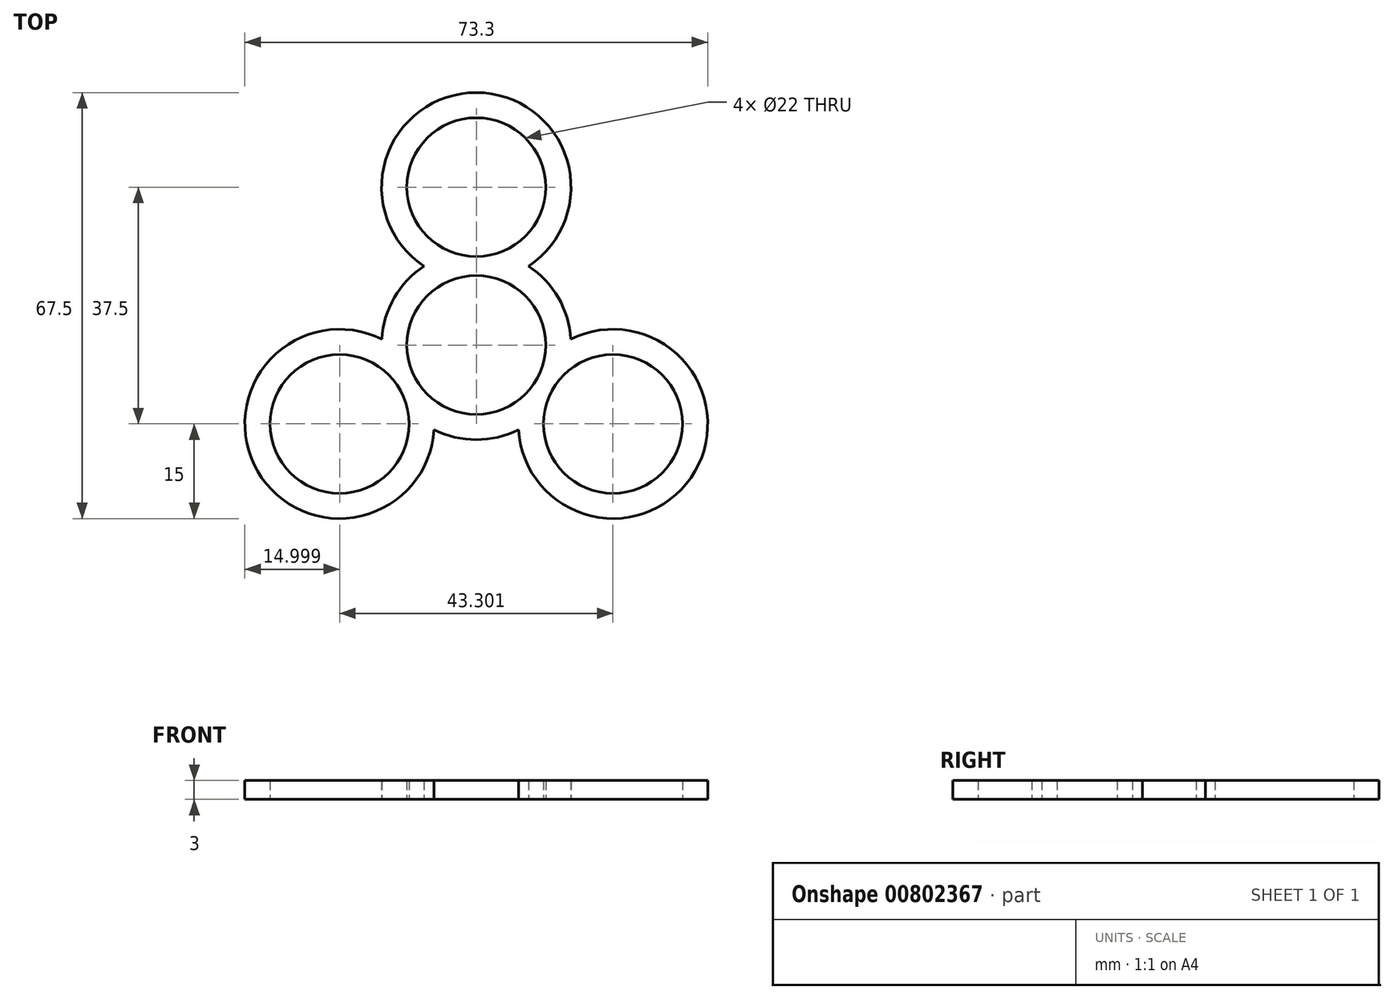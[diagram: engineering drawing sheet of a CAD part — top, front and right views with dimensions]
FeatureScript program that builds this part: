
annotation { "Feature Type Name" : "Feature", "Feature Type Description" : "" }
export const myFeature = defineFeature(function(context is Context, id is Id, definition is map)
    precondition{}
    {
        {
            var Q0;
            Q0=qCreatedBy(makeId("Top.planeOp"),FACE);
            var sketch = newSketch(context, id + "F0", { "sketchPlane" : qUnion([Q0])});
            skArc(sketch, "E0", {"start": v(9.53, 5.5) * mm, "mid": v(0, 11) * mm, "end": v(-9.53, 5.5) * mm});
            skCircle(sketch, "E1", {"center": v(0, 25) * mm, "radius": 11 * mm});
            skArc(sketch, "E2", {"start": v(8.3, 12.5) * mm, "mid": v(0, 40) * mm, "end": v(-8.3, 12.5) * mm});
            skArc(sketch, "E3", {"start": v(-8.3, 12.5) * mm, "mid": v(-10.93, 10.27) * mm, "end": v(-13, 7.5) * mm});
            skArc(sketch, "E4.trimOffspring", {"start": v(13, 7.5) * mm, "mid": v(10.93, 10.27) * mm, "end": v(8.3, 12.5) * mm});
            skArc(sketch, "E5.1.0", {"start": v(-9.53, 5.5) * mm, "mid": v(-9.53, -5.5) * mm, "end": v(0, -11) * mm});
            skArc(sketch, "E5.1.1", {"start": v(-14.97, 0.93) * mm, "mid": v(-34.64, -20) * mm, "end": v(-6.68, -13.43) * mm});
            skArc(sketch, "E5.1.2", {"start": v(-6.68, -13.43) * mm, "mid": v(-3.43, -14.6) * mm, "end": v(0, -15) * mm});
            skArc(sketch, "E5.1.3", {"start": v(-13, 7.5) * mm, "mid": v(-14.36, 4.33) * mm, "end": v(-14.97, 0.93) * mm});
            skCircle(sketch, "E5.1.4", {"center": v(-21.65, -12.5) * mm, "radius": 11 * mm});
            skArc(sketch, "E5.2.0", {"start": v(0, -11) * mm, "mid": v(9.53, -5.5) * mm, "end": v(9.53, 5.5) * mm});
            skArc(sketch, "E5.2.1", {"start": v(6.68, -13.43) * mm, "mid": v(34.64, -20) * mm, "end": v(14.97, 0.93) * mm});
            skArc(sketch, "E5.2.2", {"start": v(14.97, 0.93) * mm, "mid": v(14.36, 4.33) * mm, "end": v(13, 7.5) * mm});
            skArc(sketch, "E5.2.3", {"start": v(0, -15) * mm, "mid": v(3.43, -14.6) * mm, "end": v(6.68, -13.43) * mm});
            skCircle(sketch, "E5.2.4", {"center": v(21.65, -12.5) * mm, "radius": 11 * mm});
            skSolve(sketch);
        }
        {
            var Q0;
            Q0 = qSketchRegion(id + "F0", true);
            extrude(context, id + "F1", {"entities" : qUnion([Q0]), "depth" : 3 * mm, "offsetDistance" : 25 * mm});
        }
    });
